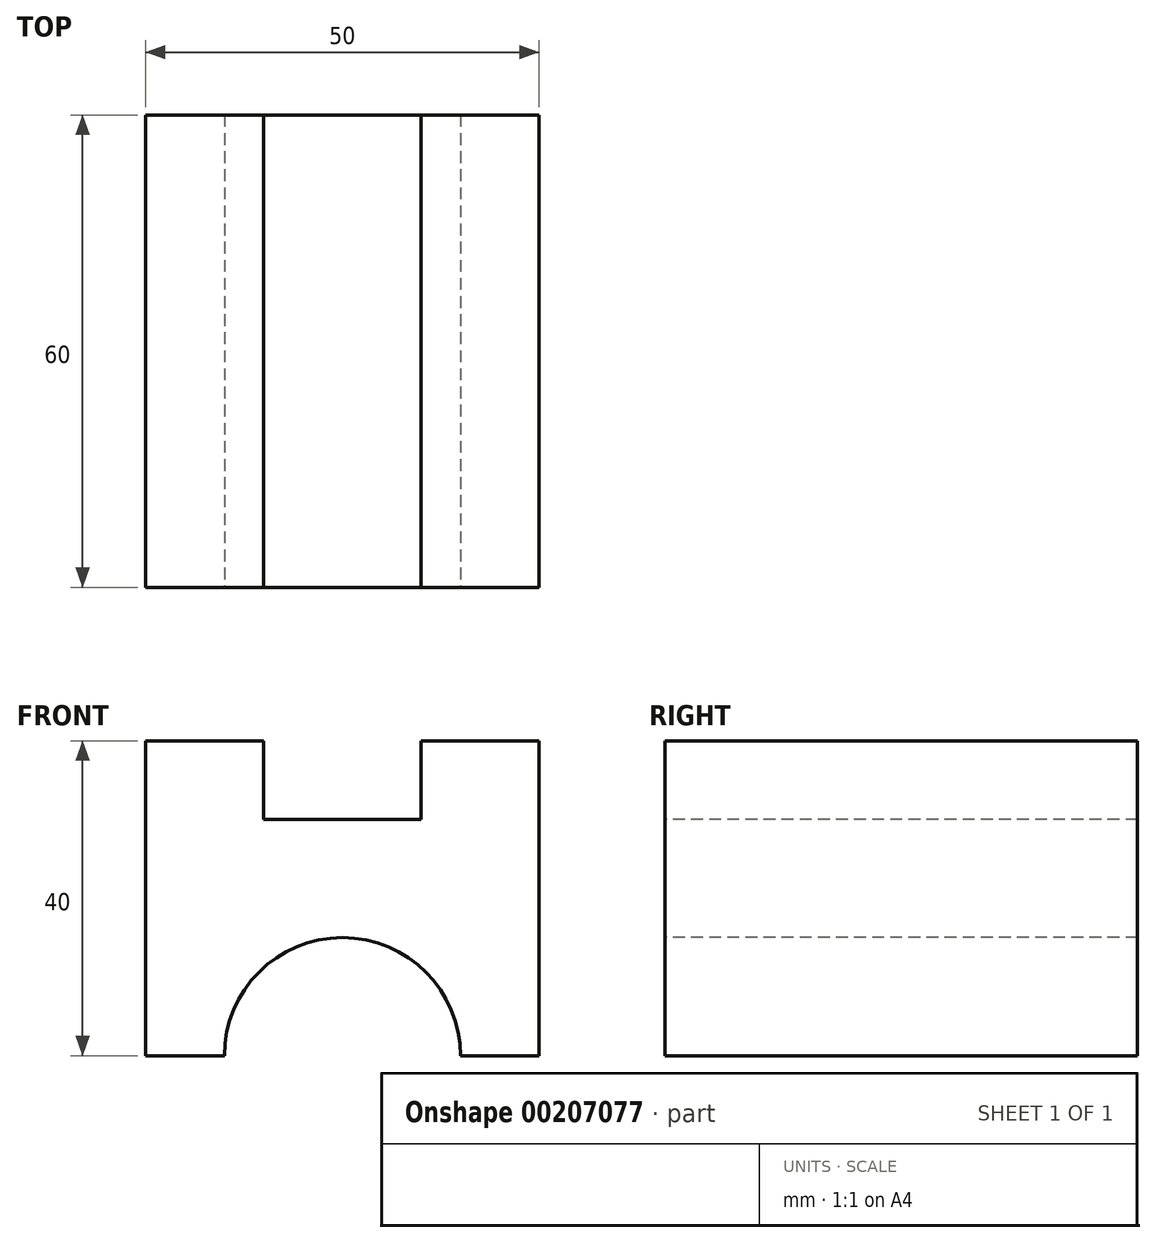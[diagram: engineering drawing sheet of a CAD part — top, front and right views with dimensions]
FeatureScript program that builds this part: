
annotation { "Feature Type Name" : "Feature", "Feature Type Description" : "" }
export const myFeature = defineFeature(function(context is Context, id is Id, definition is map)
    precondition{}
    {
        {
            var Q0;
            Q0=qCreatedBy(makeId("Front.planeOp"),FACE);
            var sketch = newSketch(context, id + "F0", { "sketchPlane" : qUnion([Q0])});
            skLineSegment(sketch, "E0", {"start": v(0, 0) * mm, "end": v(50, 0) * mm});
            skLineSegment(sketch, "E1", {"start": v(50, 0) * mm, "end": v(50, 40) * mm});
            skLineSegment(sketch, "E2", {"start": v(50, 40) * mm, "end": v(35, 40) * mm});
            skLineSegment(sketch, "E3", {"start": v(35, 40) * mm, "end": v(35, 30) * mm});
            skLineSegment(sketch, "E4", {"start": v(35, 30) * mm, "end": v(15, 30) * mm});
            skLineSegment(sketch, "E5", {"start": v(15, 30) * mm, "end": v(15, 40) * mm});
            skLineSegment(sketch, "E6", {"start": v(15, 40) * mm, "end": v(0, 40) * mm});
            skLineSegment(sketch, "E7", {"start": v(0, 40) * mm, "end": v(0, 0) * mm});
            skArc(sketch, "E8", {"start": v(40, 0) * mm, "mid": v(25, 15) * mm, "end": v(10, 0) * mm});
            skSolve(sketch);
        }
        {
            var Q0;
            {var subQ0=sQuery(id+"F0.wireOp",EDGE,"E1");Q0=makeQuery(id+"F0.imprint","IMPRINT",FACE,{"disambiguationData":[TD([[makeQuery(id+"F0.imprint","IMPRINT",EDGE,{"derivedFrom":subQ0}),1.0]])]});}
            extrude(context, id + "F1", {"entities" : qUnion([Q0]), "oppositeDirection" : true, "depth" : 60 * mm});
        }
    });
